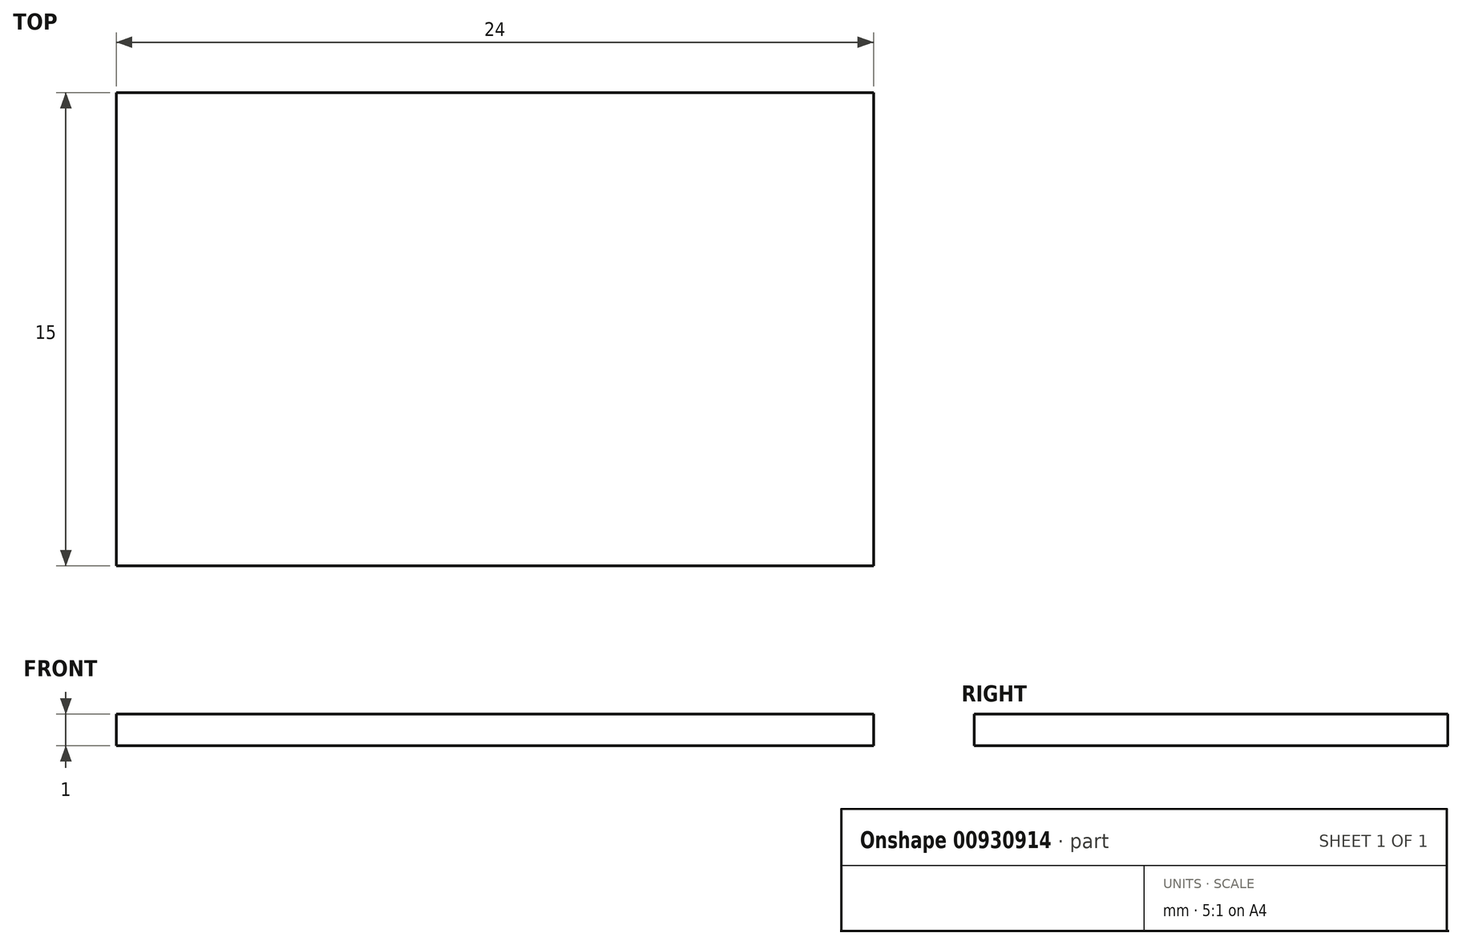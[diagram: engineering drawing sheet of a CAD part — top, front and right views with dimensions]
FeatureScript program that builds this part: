
annotation { "Feature Type Name" : "Feature", "Feature Type Description" : "" }
export const myFeature = defineFeature(function(context is Context, id is Id, definition is map)
    precondition{}
    {
        {
            var Q0;
            Q0=qCreatedBy(makeId("Top.planeOp"),FACE);
            var sketch = newSketch(context, id + "F0", { "sketchPlane" : qUnion([Q0])});
            skLineSegment(sketch, "E0.bottom", {"start": v(12, 7.5) * mm, "end": v(-12, 7.5) * mm});
            skLineSegment(sketch, "E0.top", {"start": v(12, -7.5) * mm, "end": v(-12, -7.5) * mm});
            skLineSegment(sketch, "E0.left", {"start": v(12, 7.5) * mm, "end": v(12, -7.5) * mm});
            skLineSegment(sketch, "E0.right", {"start": v(-12, 7.5) * mm, "end": v(-12, -7.5) * mm});
            skPoint(sketch, "E0.middle", {"position": v(0, 0) * mm});
            skSolve(sketch);
        }
        {
            var Q0;
            Q0=makeQuery(id+"F0.imprint","IMPRINT",FACE,{"disambiguationData":[TD([[makeQuery(id+"F0.imprint","IMPRINT",EDGE,{"derivedFrom":sQuery(id+"F0.wireOp",EDGE,"E0.bottom")}),1.0]])]});
            extrude(context, id + "F1", {"entities" : qUnion([Q0]), "depth" : 1 * mm, "offsetDistance" : 25 * mm});
        }
    });
